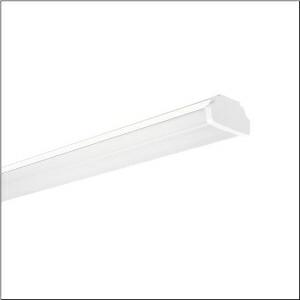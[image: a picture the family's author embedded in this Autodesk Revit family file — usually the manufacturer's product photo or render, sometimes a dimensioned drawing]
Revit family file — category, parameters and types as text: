
# Revit family: modario_31_gen_2_53bm812cv6a5d2_5516
name_source: partatom
category: Lighting Fixtures
units: mm (PartAtom-declared; Revit-internal decimal feet)

## family parameters
Cut with Voids When Loaded = No
Host = Face
Light Source = No
Part Type = Normal
Room Calculation Point = No
Round Connector Dimension = Use Diameter
Shared = No

## types (1)
- --- (1 x LED, 10550 lm, 56.5 W, 6500K)
    Apparent Load = 57 VA
    CIE Flux Codes = 47 80 95 93 100
    Color Rendering = 80
    Color Temperature = 6500K
    Default Elevation = 1800 mm
    Description = Modario 31 Gen.2, luminaire insert, of sheet steel, coil coated, white, length: 1.495mm, width: 81mm, height: 82mm, 5x system unit, system units: 299mm, LED rated luminous flux: 10.550lm, light colour: 865, SDCM (Standard Deviation of Colour Matching)MacAdam ≤ 3 SDCM (initial), control gear: ON/OFF Multilumen, CLOi, with plug, 3-pole, with phase selection, mains connection: 220..240V, AC, 50/60Hz, start of lifetime: 57W, end of service life: 68W, through-wiring accessed according to module size, primary optical cover: cover, of PMMA, light emission: direct distribution, primary light characteristic: symmetric, protection rating (complete): IP20, protection rating (LED compartment): IP50, insulation class (complete): insulation class I (protective earthing), certification: CE, ENEC, VDE, UKCA, impact resistance: IK03, permissible ambient temperature for indoor applications: -35..+40°C, corresponds to IFS (International Featured Standards) requirements for safety and quality in the food industry, reducing of maximum allowable ambient temperature of 5°C with ceiling mounting, IP40 when using the optional accessory 5TP9018, packaging unit: 1 piece
    Height = 92 mm
    Lamp = 1 x LED
    Lamp Light Flux = 10550 lm
    Lamp Power = 56.5 W
    Lamp count = 1
    Length = 1495 mm
    Luminous efficacy = 187 lm/W
    Manufacturer = Siteco
    ModVariant = No
    Model = 53BM812CV6A5D2
    Mounting Place = Ceiling
    Mounting Type = Pendant
    Number of Poles = 1
    OnlyDefault = Yes
    Power Factor = 1
    Product Name = Modario 31 Gen.2
    Product group = luminaire insert | ceiling pendant
    ProductGroupID = 901
    Protection Class = Protection class I
    Protection Degree = IP 20
    RLX_Detail_Level = 1
    RLX_Emergency_Light_Flux = 0 lm
    RLX_Emergency_Type = 0
    RLX_Emergency_Type_DB = No
    RlxData = <blob elided: 40089 chars, md5=8a2bab5d>
    Socket = socket
    Standby Power = 0 W
    System Light Flux = 10550 lm
    System Power = 57 W
    Type Comments = factory setting: luminous flux: 100 % | (A | C | E) | 133 mA
    Type Image = l_1341886.jpg
    URL = http://relux.com
    VarID = @adj_040707
    Voltage = 0 V
    Weight = 0.00 kg
    Width = 81 mm

## geometry (parser evidence)
native form markers: Blend x4, Sweep x11
no freeform markers — native parametric forms only
